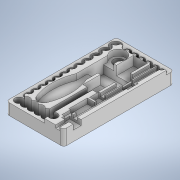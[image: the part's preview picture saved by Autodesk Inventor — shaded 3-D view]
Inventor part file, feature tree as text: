
AUTODESK INVENTOR PART (.ipt)
format: ipt  version: 2020 (Build 240168000, 168)  size: 549,376 bytes
history: native  units: mm
features: extrude x12, sketch x12, fillet x11
ambient origin geometry x8: Origin, YZ Plane, XZ Plane, XY Plane, X Axis, Y Axis, Z Axis, Center Point
bodies: Solide1 (feature_tree)
feature tree (35):
  extrude  "Extrusion1"  Depth=100.0mm
  fillet  "Congé1"  Radius=191.0mm
  extrude  "Extrusion2"  Depth=26.5mm TaperAngle=0.0deg
  extrude  "Extrusion3"  Depth=5.0mm
  fillet  "Congé2"  Radius=15.5mm
  fillet  "Congé3"  Radius=13.0mm
  extrude  "Extrusion4"  Depth=13.0mm
  fillet  "Congé4"  Radius=66.5mm
  fillet  "Congé5"  Radius=7.0mm
  fillet  "Congé6"  Radius=30.0mm
  extrude  "Extrusion5"  Depth=14.0mm
  fillet  "Congé7"  Radius=12.0mm
  fillet  "Congé8"  Radius=13.0mm
  fillet  "Congé9"  Radius=12.0mm
  extrude  "Extrusion6"  Depth=12.0mm
  extrude  "Extrusion7"  Depth=12.0mm
  sketch  "Esquisse9"
  extrude  "Extrusion8"  Depth=12.0mm
  extrude  "Extrusion9"  Depth=10.0mm
  extrude  "Extrusion10"  Depth=13.5mm
  extrude  "Extrusion11"  Depth=7.0mm
  extrude  "Extrusion12"  Depth=7.0mm
  fillet  "Congé12"  Radius=7.0mm
  fillet  "Congé13"  Radius=7.0mm
  sketch  "Esquisse1"
  sketch  "Esquisse2"
  sketch  "Esquisse4"
  sketch  "Esquisse5"
  sketch  "Esquisse6"
  sketch  "Esquisse7"
  sketch  "Esquisse8"
  sketch  "Esquisse10"
  sketch  "Esquisse11"
  sketch  "Esquisse12"
  sketch  "Esquisse13"
